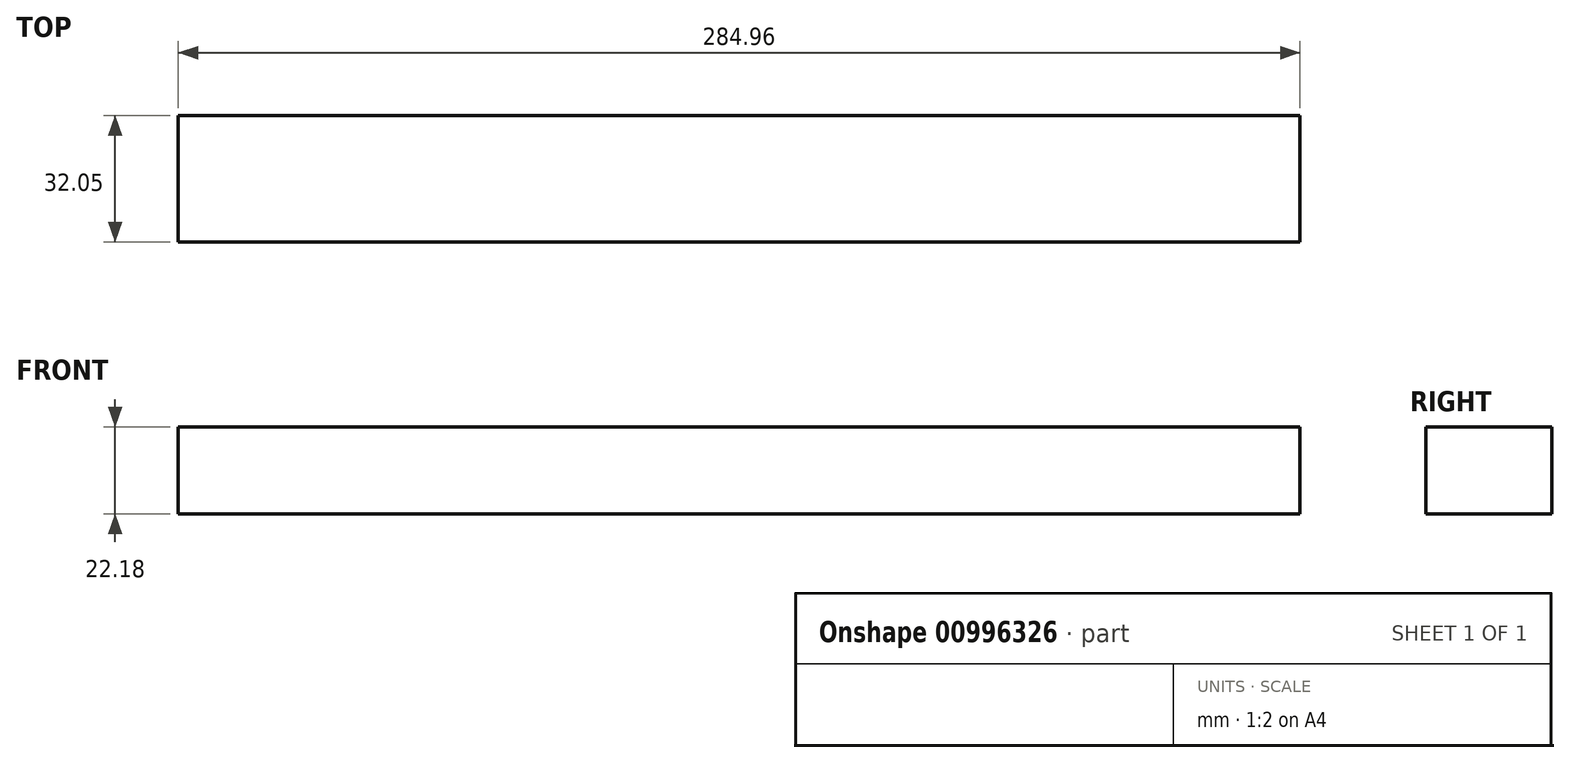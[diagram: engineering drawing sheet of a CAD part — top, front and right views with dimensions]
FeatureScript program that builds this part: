
annotation { "Feature Type Name" : "Feature", "Feature Type Description" : "" }
export const myFeature = defineFeature(function(context is Context, id is Id, definition is map)
    precondition{}
    {
        {
            var Q0;
            Q0=qCreatedBy(makeId("Front.planeOp"),FACE);
            var sketch = newSketch(context, id + "F0", { "sketchPlane" : qUnion([Q0])});
            skLineSegment(sketch, "E0.bottom", {"start": v(142.48, -11.09) * mm, "end": v(-142.48, -11.09) * mm});
            skLineSegment(sketch, "E0.top", {"start": v(142.48, 11.09) * mm, "end": v(-142.48, 11.09) * mm});
            skLineSegment(sketch, "E0.left", {"start": v(142.48, -11.09) * mm, "end": v(142.48, 11.09) * mm});
            skLineSegment(sketch, "E0.right", {"start": v(-142.48, -11.09) * mm, "end": v(-142.48, 11.09) * mm});
            skPoint(sketch, "E0.middle", {"position": v(0, 0) * mm});
            skSolve(sketch);
        }
        {
            var Q0;
            Q0=makeQuery(id+"F0.imprint","IMPRINT",FACE,{"disambiguationData":[TD([[makeQuery(id+"F0.imprint","IMPRINT",EDGE,{"derivedFrom":sQuery(id+"F0.wireOp",EDGE,"E0.bottom")}),-1.0]])]});
            extrude(context, id + "F1", {"entities" : qUnion([Q0]), "depth" : 32.05 * mm, "offsetDistance" : 25.4 * mm});
        }
    });
